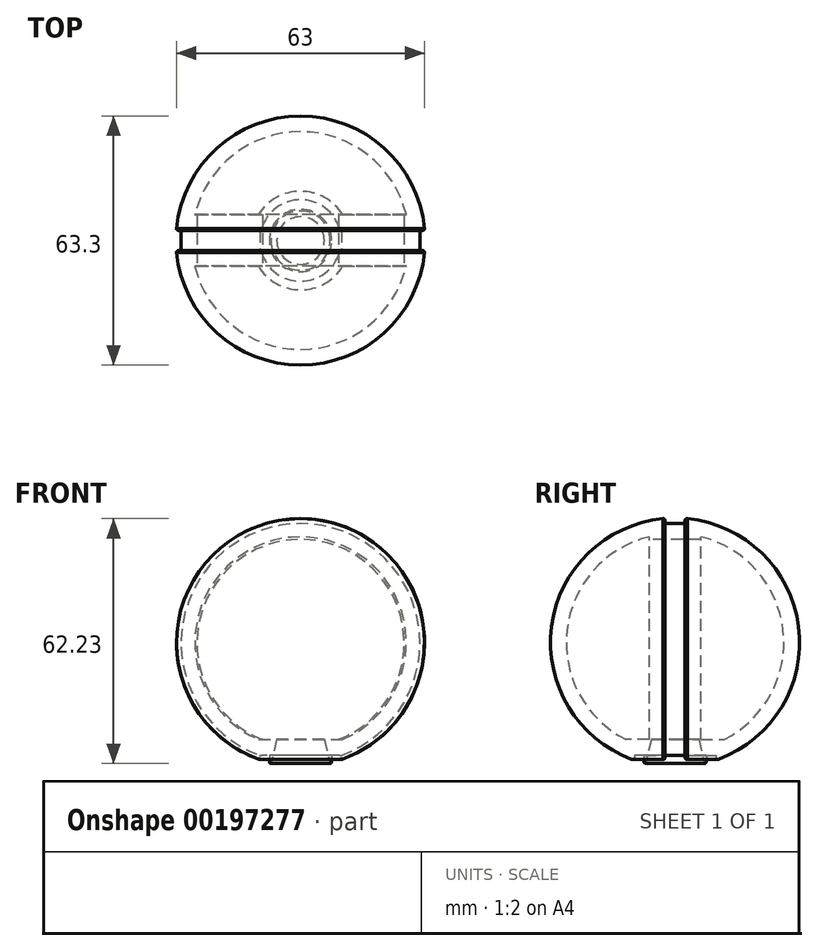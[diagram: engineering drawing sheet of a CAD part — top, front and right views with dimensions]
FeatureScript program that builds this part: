
annotation { "Feature Type Name" : "Feature", "Feature Type Description" : "" }
export const myFeature = defineFeature(function(context is Context, id is Id, definition is map)
    precondition{}
    {
        {
            var Q0;
            Q0=qCreatedBy(makeId("Front.planeOp"),FACE);
            var sketch = newSketch(context, id + "F0", { "sketchPlane" : qUnion([Q0])});
            skLineSegment(sketch, "E0", {"start": v(0, 0) * mm, "end": v(0, 63.3) * mm});
            skArc(sketch, "E1", {"start": v(0, 63.3) * mm, "mid": v(-31.65, 31.65) * mm, "end": v(0, 0) * mm});
            skSolve(sketch);
        }
        {
            var Q0;
            Q0=qSketchRegion(id+"F0",true);
            var Q1;
            Q1=sQuery(id+"F0.wireOp",EDGE,"E0");
            revolve(context, id + "F1", {"entities" : qUnion([Q0]), "axis" : qUnion([Q1]), "revolveType" : RevolveType.FULL});
        }
        {
            var Q0;
            Q0=qCreatedBy(makeId("Front.planeOp"),FACE);
            var sketch = newSketch(context, id + "F2", { "sketchPlane" : qUnion([Q0])});
            skLineSegment(sketch, "E2", {"start": v(10, -3.8) * mm, "end": v(10, 2.88) * mm});
            skLineSegment(sketch, "E3", {"start": v(-10, 2.88) * mm, "end": v(-10, -3.8) * mm});
            skLineSegment(sketch, "E4", {"start": v(0, 0) * mm, "end": v(0, 63.04) * mm, "construction": true});
            skArc(sketch, "E5", {"start": v(10, 2.88) * mm, "mid": v(0, 61.85) * mm, "end": v(-10, 2.88) * mm});
            skArc(sketch, "E6", {"start": v(10, -3.8) * mm, "mid": v(0, 68.23) * mm, "end": v(-10, -3.8) * mm});
            skSolve(sketch);
        }
        {
            var Q0;
            Q0=qSketchRegion(id+"F2",true);
            extrude(context, id + "F3", {"entities" : qUnion([Q0]), "operationType" : NewBodyOperationType.REMOVE, "oppositeDirection" : true, "depth" : 2.54 * mm, "hasSecondDirection" : true, "secondDirectionOppositeDirection" : false, "secondDirectionDepth" : 2.54 * mm});
        }
        {
            var Q0;
            Q0=qSketchRegion(id+"F2",true);
            extrude(context, id + "F4", {"entities" : qUnion([Q0]), "operationType" : NewBodyOperationType.REMOVE, "oppositeDirection" : true, "depth" : 2 * mm, "hasSecondDirection" : true, "secondDirectionOppositeDirection" : false, "secondDirectionDepth" : 2 * mm});
        }
        {
            var Q0;
            Q0=makeQuery(id+"F3.boolean.opBoolean","INTERSECT",EDGE,{"derivedFrom":[makeQuery(id+"F1.opRevolve","SWEPT_FACE",FACE,{"disambiguationData":[OSD([sQuery(id+"F0.wireOp",EDGE,"E1")])]}),makeQuery(id+"F3.opExtrude","CAP_FACE",FACE,{"disambiguationData":[OSD([sQuery(id+"F2.wireOp",EDGE,"E2"),sQuery(id+"F2.wireOp",EDGE,"E3"),sQuery(id+"F2.wireOp",EDGE,"E5"),sQuery(id+"F2.wireOp",EDGE,"E6")])],"isStart":true})]});
            var Q1;
            Q1=makeQuery(id+"F3.boolean.opBoolean","INTERSECT",EDGE,{"derivedFrom":[makeQuery(id+"F1.opRevolve","SWEPT_FACE",FACE,{"disambiguationData":[OSD([sQuery(id+"F0.wireOp",EDGE,"E1")])]}),makeQuery(id+"F3.opExtrude","CAP_FACE",FACE,{"disambiguationData":[OSD([sQuery(id+"F2.wireOp",EDGE,"E2"),sQuery(id+"F2.wireOp",EDGE,"E3"),sQuery(id+"F2.wireOp",EDGE,"E5"),sQuery(id+"F2.wireOp",EDGE,"E6")])],"isStart":false})]});
            fillet(context, id + "F5", {"entities" : qUnion([Q0, Q1]), "radius" : .5 * mm, "tangentPropagation" : true, "allowEdgeOverflow" : false});
        }
        {
            var Q0;
            Q0=makeQuery(id+"F3.boolean.opBoolean","INTERSECT",EDGE,{"derivedFrom":[makeQuery(id+"F1.opRevolve","SWEPT_FACE",FACE,{"disambiguationData":[OSD([sQuery(id+"F0.wireOp",EDGE,"E1")])]}),makeQuery(id+"F3.opExtrude","SWEPT_FACE",FACE,{"disambiguationData":[OSD([sQuery(id+"F2.wireOp",EDGE,"E2")])]})]});
            var Q1;
            Q1=makeQuery(id+"F3.boolean.opBoolean","INTERSECT",EDGE,{"derivedFrom":[makeQuery(id+"F1.opRevolve","SWEPT_FACE",FACE,{"disambiguationData":[OSD([sQuery(id+"F0.wireOp",EDGE,"E1")])]}),makeQuery(id+"F3.opExtrude","SWEPT_FACE",FACE,{"disambiguationData":[OSD([sQuery(id+"F2.wireOp",EDGE,"E3")])]})]});
            fillet(context, id + "F6", {"entities" : qUnion([Q0, Q1]), "radius" : .2 * mm, "tangentPropagation" : true, "allowEdgeOverflow" : false});
        }
        {
            var Q0;
            Q0=qCreatedBy(makeId("Top.planeOp"),FACE);
            var sketch = newSketch(context, id + "F7", { "sketchPlane" : qUnion([Q0])});
            skCircle(sketch, "E7", {"center": v(0, 0) * mm, "radius": 10.36 * mm});
            skCircle(sketch, "E8", {"center": v(0, 0) * mm, "radius": 7.92 * mm});
            skSolve(sketch);
        }
        {
            var Q0;
            Q0=qSketchRegion(id+"F7",true);
            extrude(context, id + "F8", {"entities" : qUnion([Q0]), "operationType" : NewBodyOperationType.REMOVE, "depth" : 3 * mm});
        }
        {
            var Q0;
            Q0=makeQuery(id+"F8.boolean.opBoolean","INTERSECT",EDGE,{"disambiguationData":[OD(0.0)],"derivedFrom":[makeQuery(id+"F1.opRevolve","SWEPT_FACE",FACE,{"disambiguationData":[OSD([sQuery(id+"F0.wireOp",EDGE,"E1")])]}),makeQuery(id+"F8.opExtrude","SWEPT_FACE",FACE,{"disambiguationData":[OSD([sQuery(id+"F7.wireOp",EDGE,"E7")])]})]});
            var Q1;
            Q1=makeQuery(id+"F8.boolean.opBoolean","INTERSECT",EDGE,{"disambiguationData":[OD(1.0)],"derivedFrom":[makeQuery(id+"F1.opRevolve","SWEPT_FACE",FACE,{"disambiguationData":[OSD([sQuery(id+"F0.wireOp",EDGE,"E1")])]}),makeQuery(id+"F8.opExtrude","SWEPT_FACE",FACE,{"disambiguationData":[OSD([sQuery(id+"F7.wireOp",EDGE,"E7")])]})]});
            fillet(context, id + "F9", {"entities" : qUnion([Q0, Q1]), "radius" : .5 * mm, "tangentPropagation" : true, "allowEdgeOverflow" : false});
        }
        {
            var Q0;
            Q0=makeQuery(id+"F8.boolean.opBoolean","INTERSECT",EDGE,{"derivedFrom":[makeQuery(id+"F1.opRevolve","SWEPT_FACE",FACE,{"disambiguationData":[OSD([sQuery(id+"F0.wireOp",EDGE,"E1")])]}),makeQuery(id+"F8.opExtrude","SWEPT_FACE",FACE,{"disambiguationData":[OSD([sQuery(id+"F7.wireOp",EDGE,"E8")])]})]});
            fillet(context, id + "F10", {"entities" : qUnion([Q0]), "radius" : .5 * mm, "tangentPropagation" : true, "allowEdgeOverflow" : false});
        }
        {
            var Q0;
            Q0=makeQuery(id+"F8.boolean.opBoolean","SPLIT",FACE,{"disambiguationData":[TD([makeQuery(id+"F8.opExtrude","SWEPT_FACE",FACE,{"disambiguationData":[OSD([sQuery(id+"F7.wireOp",EDGE,"E8")])]})])],"derivedFrom":makeQuery(id+"F1.opRevolve","SWEPT_FACE",FACE,{"disambiguationData":[OSD([sQuery(id+"F0.wireOp",EDGE,"E1")])]})});
            shell(context, id + "F11", {"entities" : qUnion([Q0]), "thickness" : 4 * mm});
        }
    });
